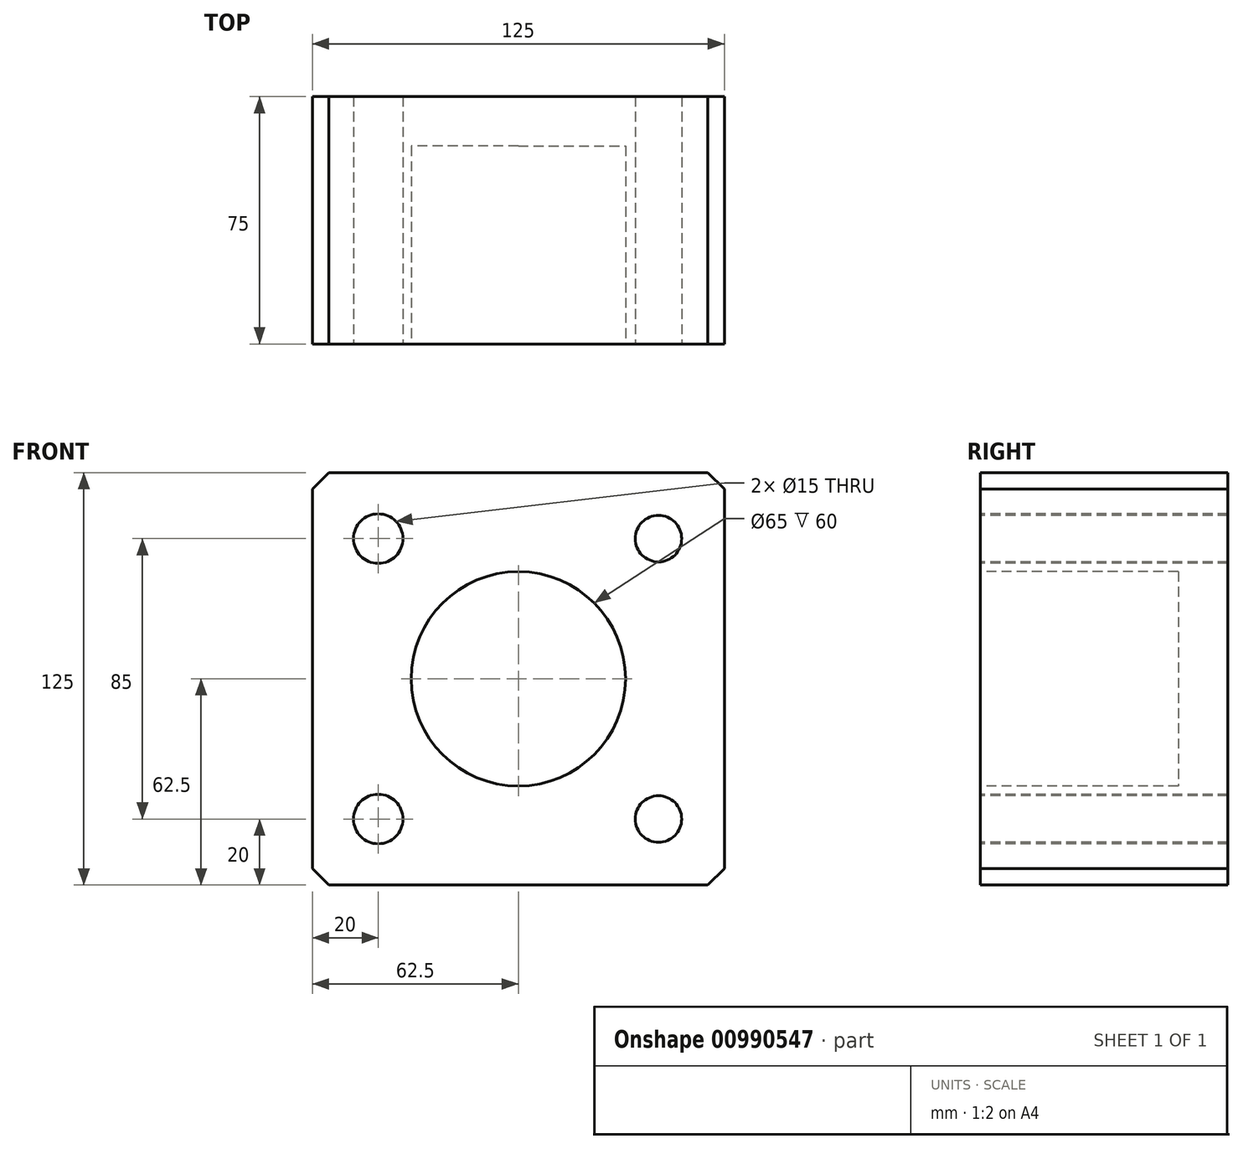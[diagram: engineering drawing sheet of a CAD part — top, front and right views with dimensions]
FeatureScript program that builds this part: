
annotation { "Feature Type Name" : "Feature", "Feature Type Description" : "" }
export const myFeature = defineFeature(function(context is Context, id is Id, definition is map)
    precondition{}
    {
        {
            var Q0;
            Q0=qCreatedBy(makeId("Front.planeOp"),FACE);
            var sketch = newSketch(context, id + "F0", { "sketchPlane" : qUnion([Q0])});
            skLineSegment(sketch, "E0.bottom", {"start": v(62.5, -62.5) * mm, "end": v(-62.5, -62.5) * mm});
            skLineSegment(sketch, "E0.top", {"start": v(62.5, 62.5) * mm, "end": v(-62.5, 62.5) * mm});
            skLineSegment(sketch, "E0.left", {"start": v(62.5, -62.5) * mm, "end": v(62.5, 62.5) * mm});
            skLineSegment(sketch, "E0.right", {"start": v(-62.5, -62.5) * mm, "end": v(-62.5, 62.5) * mm});
            skPoint(sketch, "E0.middle", {"position": v(0, 0) * mm});
            skSolve(sketch);
        }
        {
            var Q0;
            Q0=qSketchRegion(id+"F0",true);
            extrude(context, id + "F1", {"entities" : qUnion([Q0]), "depth" : 75 * mm, "offsetDistance" : 25 * mm});
        }
        {
            var Q0;
            Q0=makeQuery(id+"F1.opExtrude","SWEPT_EDGE",EDGE,{"disambiguationData":[OSD([sQuery(id+"F0.wireOp",EDGE,"E0.top"),sQuery(id+"F0.wireOp",EDGE,"E0.left")])]});
            var Q1;
            Q1=makeQuery(id+"F1.opExtrude","SWEPT_EDGE",EDGE,{"disambiguationData":[OSD([sQuery(id+"F0.wireOp",EDGE,"E0.top"),sQuery(id+"F0.wireOp",EDGE,"E0.right")])]});
            var Q2;
            Q2=makeQuery(id+"F1.opExtrude","SWEPT_EDGE",EDGE,{"disambiguationData":[OSD([sQuery(id+"F0.wireOp",EDGE,"E0.bottom"),sQuery(id+"F0.wireOp",EDGE,"E0.left")])]});
            var Q3;
            Q3=makeQuery(id+"F1.opExtrude","SWEPT_EDGE",EDGE,{"disambiguationData":[OSD([sQuery(id+"F0.wireOp",EDGE,"E0.bottom"),sQuery(id+"F0.wireOp",EDGE,"E0.right")])]});
            chamfer(context, id + "F2", {"entities" : qUnion([Q0, Q1, Q2, Q3]), "width" : 5 * mm, "tangentPropagation" : true});
        }
        {
            var Q0;
            Q0=makeQuery(id+"F1.opExtrude","CAP_FACE",FACE,{"disambiguationData":[OSD([sQuery(id+"F0.wireOp",EDGE,"E0.bottom"),sQuery(id+"F0.wireOp",EDGE,"E0.top"),sQuery(id+"F0.wireOp",EDGE,"E0.left"),sQuery(id+"F0.wireOp",EDGE,"E0.right")])],"isStart":false});
            var sketch = newSketch(context, id + "F3", { "sketchPlane" : qUnion([Q0])});
            skLineSegment(sketch, "E1.bottom", {"start": v(42.5, 42.5) * mm, "end": v(-42.5, 42.5) * mm, "construction": true});
            skLineSegment(sketch, "E1.top", {"start": v(42.5, -42.5) * mm, "end": v(-42.5, -42.5) * mm, "construction": true});
            skLineSegment(sketch, "E1.left", {"start": v(42.5, 42.5) * mm, "end": v(42.5, -42.5) * mm, "construction": true});
            skLineSegment(sketch, "E1.right", {"start": v(-42.5, 42.5) * mm, "end": v(-42.5, -42.5) * mm, "construction": true});
            skPoint(sketch, "E1.middle", {"position": v(0, 0) * mm});
            skCircle(sketch, "E2", {"center": v(-42.5, 42.5) * mm, "radius": 7.5 * mm});
            skCircle(sketch, "E3", {"center": v(-42.5, -42.5) * mm, "radius": 7.5 * mm});
            skCircle(sketch, "E4", {"center": v(42.5, -42.5) * mm, "radius": 7.04 * mm});
            skCircle(sketch, "E5", {"center": v(42.5, 42.5) * mm, "radius": 7.04 * mm});
            skSolve(sketch);
        }
        {
            var Q0;
            Q0=qSketchRegion(id+"F3",true);
            extrude(context, id + "F4", {"entities" : qUnion([Q0]), "operationType" : NewBodyOperationType.REMOVE, "endBound" : BoundingType.THROUGH_ALL, "oppositeDirection" : true, "depth" : 25 * mm, "offsetDistance" : 25 * mm});
        }
        {
            var Q0;
            Q0=makeQuery(id+"F1.opExtrude","CAP_FACE",FACE,{"disambiguationData":[OSD([sQuery(id+"F0.wireOp",EDGE,"E0.bottom"),sQuery(id+"F0.wireOp",EDGE,"E0.top"),sQuery(id+"F0.wireOp",EDGE,"E0.left"),sQuery(id+"F0.wireOp",EDGE,"E0.right")])],"isStart":false});
            var sketch = newSketch(context, id + "F5", { "sketchPlane" : qUnion([Q0])});
            skCircle(sketch, "E6", {"center": v(0, 0) * mm, "radius": 32.5 * mm});
            skSolve(sketch);
        }
        {
            var Q0;
            Q0=qSketchRegion(id+"F5",true);
            extrude(context, id + "F6", {"entities" : qUnion([Q0]), "operationType" : NewBodyOperationType.REMOVE, "endBound" : BoundingType.THROUGH_ALL, "oppositeDirection" : true, "depth" : 25 * mm, "offsetDistance" : 25 * mm});
        }
        {
            var Q0;
            Q0=makeQuery(id+"F1.opExtrude","CAP_FACE",FACE,{"disambiguationData":[OSD([sQuery(id+"F0.wireOp",EDGE,"E0.bottom"),sQuery(id+"F0.wireOp",EDGE,"E0.top"),sQuery(id+"F0.wireOp",EDGE,"E0.left"),sQuery(id+"F0.wireOp",EDGE,"E0.right")])],"isStart":true});
            var sketch = newSketch(context, id + "F7", { "sketchPlane" : qUnion([Q0])});
            skCircle(sketch, "E7.0", {"center": v(0, 0) * mm, "radius": 32.5 * mm});
            skSolve(sketch);
        }
        {
            var Q0;
            Q0 = qSketchRegion(id + "F7", true);
            extrude(context, id + "F8", {"entities" : qUnion([Q0]), "operationType" : NewBodyOperationType.ADD, "oppositeDirection" : true, "depth" : 15 * mm, "offsetDistance" : 25 * mm});
        }
    });
